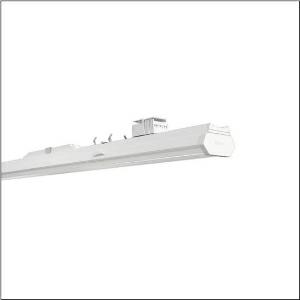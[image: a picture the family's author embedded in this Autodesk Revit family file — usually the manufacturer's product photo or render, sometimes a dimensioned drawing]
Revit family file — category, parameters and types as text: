
# Revit family: licross_r__11_protected_mo_51td1bcn485g_09c4
name_source: partatom
category: Lighting Fixtures
units: mm (PartAtom-declared; Revit-internal decimal feet)

## family parameters
Cut with Voids When Loaded = No
Host = Face
Light Source = No
Part Type = Normal
Room Calculation Point = No
Round Connector Dimension = Use Diameter
Shared = No

## types (1)
- --- (1 x LED, 8520 lm, 49.4 W, 4000K)
    Apparent Load = 49 VA
    CIE Flux Codes = 54 82 95 97 100
    Color Rendering = 80
    Color Temperature = 4000K
    Default Elevation = 1800 mm
    Description = Licross® 11 Protected MO, luminaire insert, of sheet steel, galvanised, coil coated, white, length: 1.500mm, width: 90mm, height: 101mm, LED rated luminous flux: 8.520lm, light colour: 840, control gear: ON/OFF Multilumen, CLOi, with plug, 3-pole, with phase selection, mains connection: 220..240V, AC, 50/60Hz, start of lifetime: 49W, end of service life: 55W, halogen-free wiring, primary optical cover: cover, of PMMA, light emission: direct distribution, primary light characteristic: symmetric, protection rating (complete): IP54, insulation class (complete): insulation class I (protective earthing), certification: CE, ENEC, VDE, UKCA, protection symbol: D if used in an environment with non-conductive dust loads with corresponding accessories, impact resistance: IK06, permissible ambient temperature for indoor applications: -35..+40°C, corresponds to IFS (International Featured Standards) requirements for safety and quality in the food industry, reducing of maximum allowable ambient temperature of 5°C with ceiling mounting, LABS conformity tested according to VDMA 24364:2018-05, packaging unit: 1 piece
    Height = 92 mm
    Lamp = 1 x LED
    Lamp Light Flux = 8520 lm
    Lamp Power = 49.4 W
    Lamp count = 1
    Length = 1500 mm
    Luminous efficacy = 172 lm/W
    Manufacturer = Siteco
    ModVariant = No
    Model = 51TD1BCN485G
    Mounting Place = Ceiling
    Mounting Type = Pendant
    Number of Poles = 1
    OnlyDefault = Yes
    Power Factor = 1
    Product Name = Licross® 11 Protected MO
    Product group = luminaire insert
    ProductGroupID = 902
    Protection Class = Protection class I
    Protection Degree = IP 54
    RLX_Detail_Level = 1
    RLX_Emergency_Light_Flux = 0 lm
    RLX_Emergency_Type = 0
    RLX_Emergency_Type_DB = No
    RlxData = <blob elided: 21965 chars, md5=30d37f4c>
    Socket = socket
    Standby Power = 0 W
    System Light Flux = 8520 lm
    System Power = 49 W
    Type Comments = factory setting: luminous flux: 100 % | (A | C | E) | 113 mA
    Type Image = l_1256145.jpg
    URL = http://relux.com
    VarID = @adj_086004
    Voltage = 0 V
    Weight = 0.00 kg
    Width = 88 mm

## geometry (parser evidence)
native form markers: Blend x4, Sweep x13
no freeform markers — native parametric forms only
